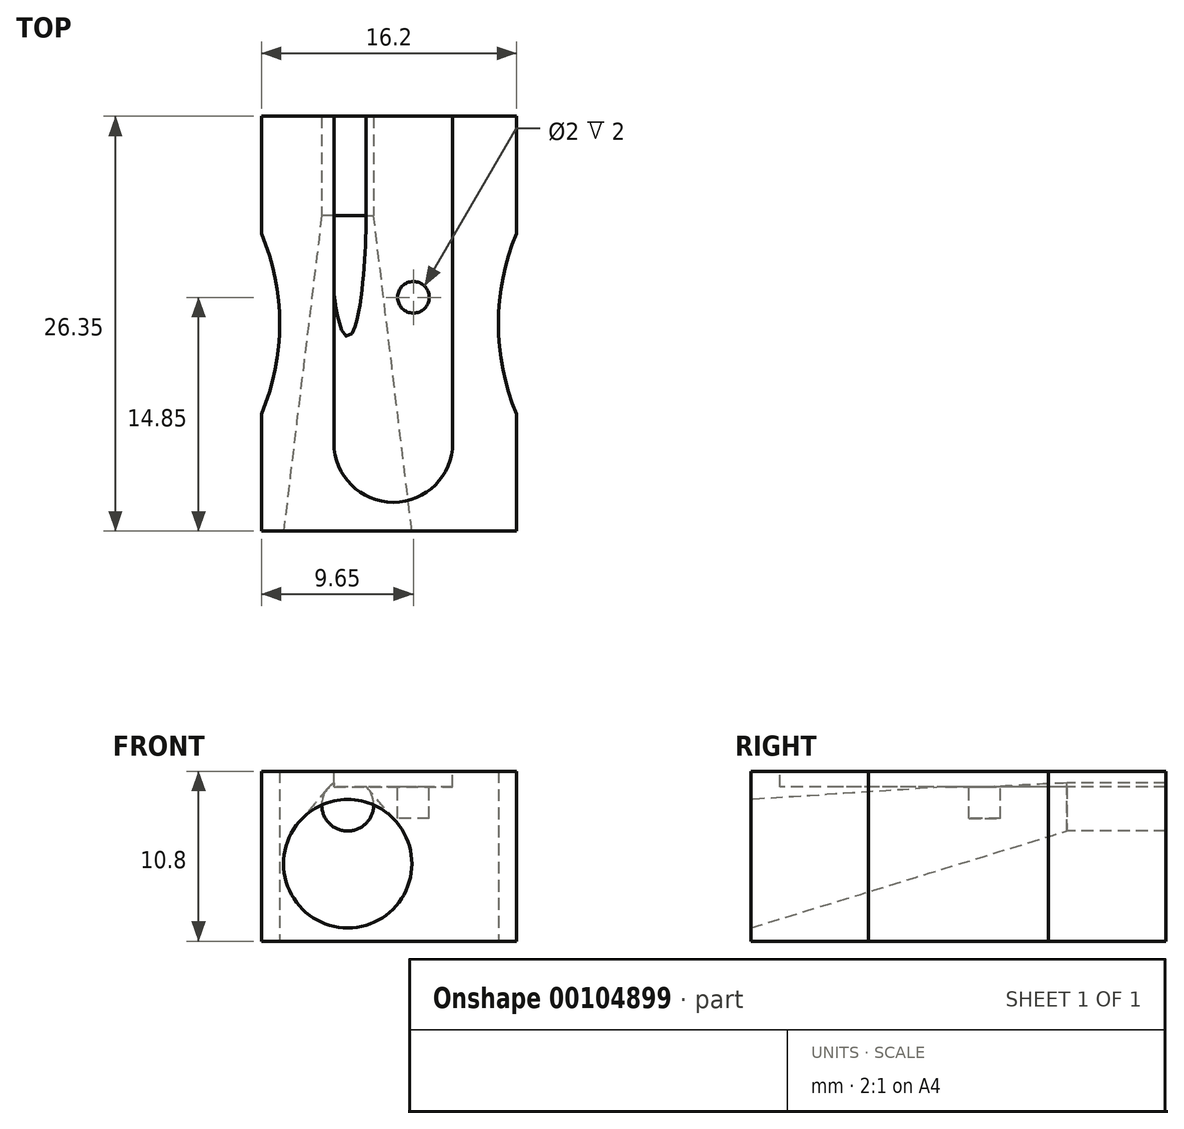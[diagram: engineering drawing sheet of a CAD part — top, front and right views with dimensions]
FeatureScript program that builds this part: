
annotation { "Feature Type Name" : "Feature", "Feature Type Description" : "" }
export const myFeature = defineFeature(function(context is Context, id is Id, definition is map)
    precondition{}
    {
        {
            var Q0;
            Q0=qCreatedBy(makeId("Top.planeOp"),FACE);
            var sketch = newSketch(context, id + "F0", { "sketchPlane" : qUnion([Q0])});
            skLineSegment(sketch, "E0", {"start": v(0, 0) * mm, "end": v(0, 26.35) * mm});
            skLineSegment(sketch, "E1", {"start": v(0, 26.35) * mm, "end": v(-8.1, 26.35) * mm});
            skLineSegment(sketch, "E2", {"start": v(-8.1, 26.35) * mm, "end": v(-8.1, 18.9) * mm});
            skLineSegment(sketch, "E3", {"start": v(-8.1, 0) * mm, "end": v(0, 0) * mm});
            skLineSegment(sketch, "E4", {"start": v(0, 13.18) * mm, "end": v(-21.65, 13.17) * mm, "construction": true});
            skArc(sketch, "E5", {"start": v(-8.1, 7.45) * mm, "mid": v(-6.94, 13.17) * mm, "end": v(-8.1, 18.9) * mm});
            skLineSegment(sketch, "E6.trimOffspring", {"start": v(-8.1, 7.45) * mm, "end": v(-8.1, 0) * mm});
            skPoint(sketch, "E7", {"position": v(-6.94, 13.17) * mm});
            skSolve(sketch);
        }
        {
            var Q0;
            Q0=qSketchRegion(id+"F0",true);
            extrude(context, id + "F1", {"entities" : qUnion([Q0]), "depth" : 10.8 * mm});
        }
        {
            var Q0;
            Q0=makeQuery(id+"F1.opExtrude","SWEPT_BODY",BODY,{"disambiguationData":[OSD([sQuery(id+"F0.wireOp",EDGE,"E0"),sQuery(id+"F0.wireOp",EDGE,"E1"),sQuery(id+"F0.wireOp",EDGE,"E2"),sQuery(id+"F0.wireOp",EDGE,"E3"),sQuery(id+"F0.wireOp",EDGE,"E5"),sQuery(id+"F0.wireOp",EDGE,"E6.trimOffspring")])]});
            var Q1;
            Q1=qCreatedBy(makeId("Right.planeOp"),FACE);
            mirror(context, id + "F2", {"operationType" : NewBodyOperationType.ADD, "entities" : qUnion([Q0]), "mirrorPlane" : qUnion([Q1])});
        }
        {
            var Q0;
            {var subQ0=makeQuery(id+"F1.opExtrude","CAP_FACE",FACE,{"disambiguationData":[OSD([sQuery(id+"F0.wireOp",EDGE,"E0"),sQuery(id+"F0.wireOp",EDGE,"E1"),sQuery(id+"F0.wireOp",EDGE,"E2"),sQuery(id+"F0.wireOp",EDGE,"E3"),sQuery(id+"F0.wireOp",EDGE,"E5"),sQuery(id+"F0.wireOp",EDGE,"E6.trimOffspring")])],"isStart":false});Q0=makeQuery(id+"F2.boolean.opBoolean","MERGE",FACE,{"derivedFrom":[subQ0,makeQuery(id+"F2.opPattern","COPY",FACE,{"derivedFrom":subQ0,"instanceName":"1"})]});}
            var sketch = newSketch(context, id + "F3", { "sketchPlane" : qUnion([Q0])});
            skLineSegment(sketch, "E8", {"start": v(-3.5, 26.35) * mm, "end": v(-3.5, 5.6) * mm});
            skLineSegment(sketch, "E9", {"start": v(4.05, 26.35) * mm, "end": v(4.05, 5.6) * mm});
            skArc(sketch, "E10", {"start": v(-3.5, 5.6) * mm, "mid": v(0.28, 1.83) * mm, "end": v(4.05, 5.6) * mm});
            skLineSegment(sketch, "E11", {"start": v(-3.5, 26.35) * mm, "end": v(4.05, 26.35) * mm});
            skSolve(sketch);
        }
        {
            var Q0;
            {var subQ0=makeQuery(id+"F1.opExtrude","SWEPT_FACE",FACE,{"disambiguationData":[OSD([sQuery(id+"F0.wireOp",EDGE,"E3")])]});Q0=makeQuery(id+"F2.boolean.opBoolean","MERGE",FACE,{"derivedFrom":[subQ0,makeQuery(id+"F2.opPattern","COPY",FACE,{"derivedFrom":subQ0,"instanceName":"1"})]});}
            var sketch = newSketch(context, id + "F4", { "sketchPlane" : qUnion([Q0])});
            skCircle(sketch, "E12", {"center": v(-2.63, 4.92) * mm, "radius": 4.08 * mm});
            skSolve(sketch);
        }
        {
            var Q0;
            {var subQ0=makeQuery(id+"F1.opExtrude","SWEPT_FACE",FACE,{"disambiguationData":[OSD([sQuery(id+"F0.wireOp",EDGE,"E1")])]});Q0=makeQuery(id+"F2.boolean.opBoolean","MERGE",FACE,{"derivedFrom":[subQ0,makeQuery(id+"F2.opPattern","COPY",FACE,{"derivedFrom":subQ0,"instanceName":"1"})]});}
            var sketch = newSketch(context, id + "F5", { "sketchPlane" : qUnion([Q0])});
            skCircle(sketch, "E13", {"center": v(2.63, 8.65) * mm, "radius": 1.65 * mm});
            skSolve(sketch);
        }
        {
            var Q0;
            {var subQ0=makeQuery(id+"F1.opExtrude","SWEPT_FACE",FACE,{"disambiguationData":[OSD([sQuery(id+"F0.wireOp",EDGE,"E1")])]});Q0=makeQuery(id+"F2.boolean.opBoolean","MERGE",FACE,{"derivedFrom":[subQ0,makeQuery(id+"F2.opPattern","COPY",FACE,{"derivedFrom":subQ0,"instanceName":"1"})]});}
            cPlane(context, id + "F6", {"entities" : qUnion([Q0]), "cplaneType" : CPlaneType.OFFSET, "offset" : 6.3 * mm, "oppositeDirection" : true, "width" : 150 * mm, "height" : 150 * mm});
        }
        {
            var Q0;
            Q0=qCreatedBy(id+"F6.planeOp",FACE);
            var sketch = newSketch(context, id + "F7", { "sketchPlane" : qUnion([Q0])});
            skCircle(sketch, "E14", {"center": v(2.63, 8.65) * mm, "radius": 1.65 * mm});
            skSolve(sketch);
        }
        {
            var Q1;
            Q1=qSketchRegion(id+"F4",true);
            var Q2;
            Q2=qSketchRegion(id+"F7",true);
            loft(context, id + "F8", {"operationType" : NewBodyOperationType.REMOVE, "sheetProfilesArray" : [{ "sheetProfileEntities" : qUnion([Q1]) }, { "sheetProfileEntities" : qUnion([Q2]) }]});
        }
        {
            var Q0;
            Q0=makeQuery(id+"F3.imprint","IMPRINT",FACE,{"disambiguationData":[TD([[makeQuery(id+"F3.imprint","IMPRINT",EDGE,{"derivedFrom":sQuery(id+"F3.wireOp",EDGE,"E8")}),1.0]])]});
            extrude(context, id + "F9", {"entities" : qUnion([Q0]), "operationType" : NewBodyOperationType.REMOVE, "oppositeDirection" : true, "depth" : 1 * mm});
        }
        {
            var Q0;
            Q0=makeQuery(id+"F9.boolean.opBoolean","COPY",FACE,{"derivedFrom":makeQuery(id+"F9.opExtrude","CAP_FACE",FACE,{"disambiguationData":[OSD([sQuery(id+"F3.wireOp",EDGE,"E8"),sQuery(id+"F3.wireOp",EDGE,"E9"),sQuery(id+"F3.wireOp",EDGE,"E10"),sQuery(id+"F3.wireOp",EDGE,"E11")])],"isStart":false})});
            var sketch = newSketch(context, id + "F10", { "sketchPlane" : qUnion([Q0])});
            skCircle(sketch, "E15", {"center": v(1.55, 14.85) * mm, "radius": 1 * mm});
            skSolve(sketch);
        }
        {
            var Q0;
            Q0=sQuery(id+"F7.wireOp",VERTEX,"E14.center");
            var Q1;
            Q1=sQuery(id+"F5.wireOp",VERTEX,"E13.center");
            var Q2;
            Q2=makeQuery(id+"F1.opExtrude","SWEPT_BODY",BODY,{"disambiguationData":[OSD([sQuery(id+"F0.wireOp",EDGE,"E0"),sQuery(id+"F0.wireOp",EDGE,"E1"),sQuery(id+"F0.wireOp",EDGE,"E2"),sQuery(id+"F0.wireOp",EDGE,"E3"),sQuery(id+"F0.wireOp",EDGE,"E5"),sQuery(id+"F0.wireOp",EDGE,"E6.trimOffspring")])]});
            hole(context, id + "F11", {"style" : HoleStyle.SIMPLE, "endStyle" : HoleEndStyle.THROUGH, "oppositeDirection" : true, "holeDiameter" : 3.3 * mm, "locations" : qUnion([Q0, Q1]), "scope" : qUnion([Q2]), "isTappedThrough" : true});
        }
        {
            var Q0;
            Q0=qSketchRegion(id+"F10",true);
            extrude(context, id + "F12", {"entities" : qUnion([Q0]), "operationType" : NewBodyOperationType.REMOVE, "oppositeDirection" : true, "depth" : 2 * mm});
        }
    });
